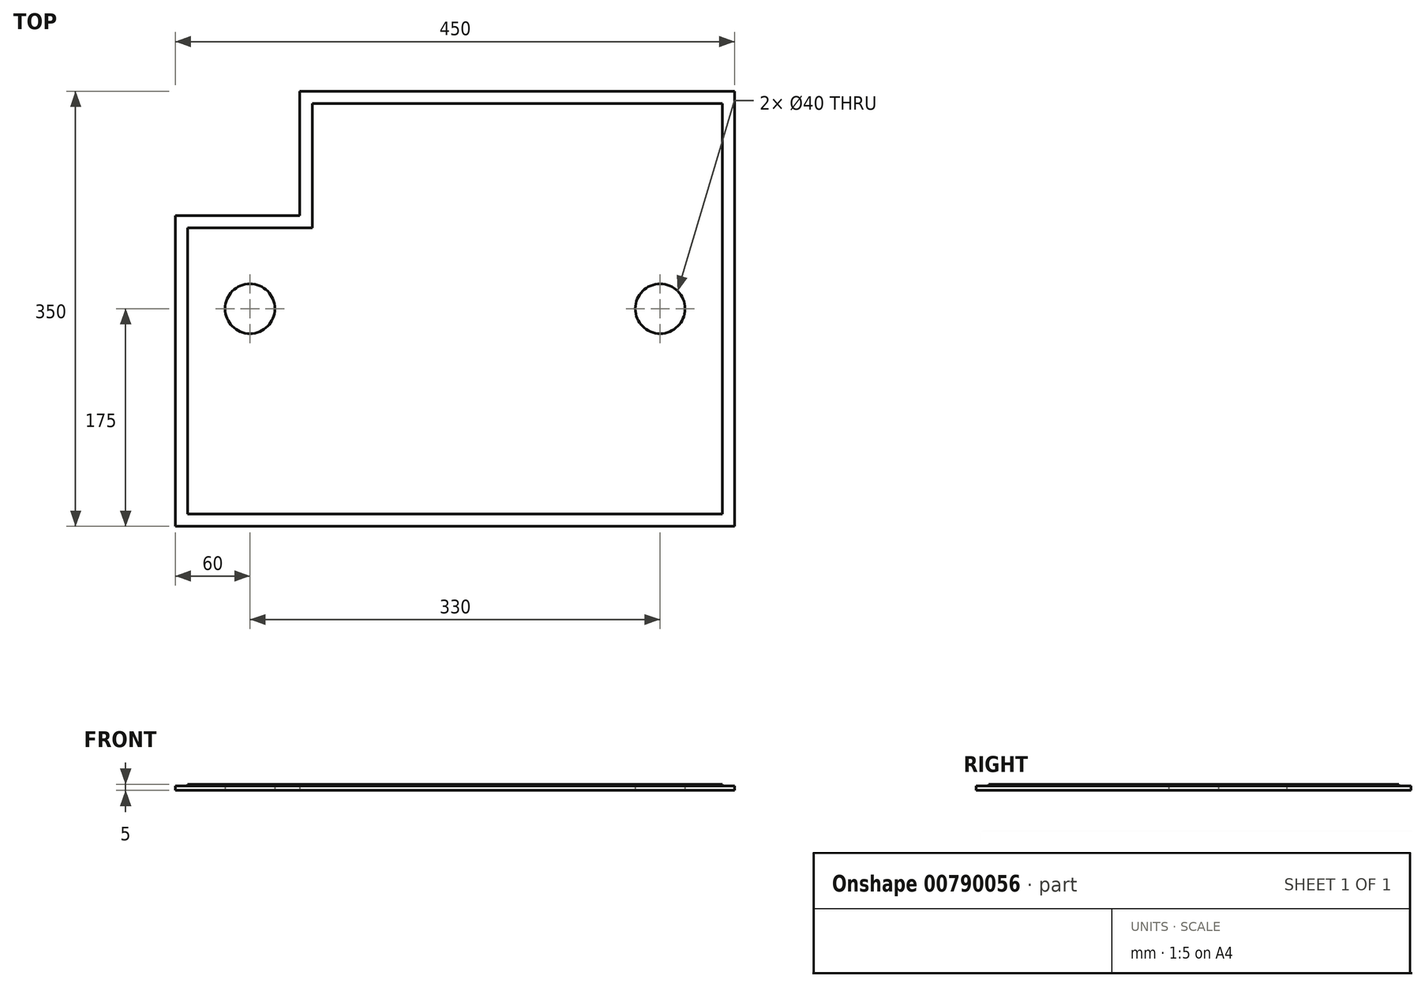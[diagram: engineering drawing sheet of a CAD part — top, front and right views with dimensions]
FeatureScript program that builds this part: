
annotation { "Feature Type Name" : "Feature", "Feature Type Description" : "" }
export const myFeature = defineFeature(function(context is Context, id is Id, definition is map)
    precondition{}
    {
        {
            var Q0;
            Q0=qCreatedBy(makeId("Top.planeOp"),FACE);
            var sketch = newSketch(context, id + "F0", { "sketchPlane" : qUnion([Q0])});
            skLineSegment(sketch, "E0", {"start": v(0, 0) * mm, "end": v(450, 0) * mm});
            skLineSegment(sketch, "E1", {"start": v(450, 0) * mm, "end": v(450, 350) * mm});
            skLineSegment(sketch, "E2", {"start": v(450, 350) * mm, "end": v(100, 350) * mm});
            skLineSegment(sketch, "E3", {"start": v(100, 350) * mm, "end": v(100, 250) * mm});
            skLineSegment(sketch, "E4", {"start": v(100, 250) * mm, "end": v(0, 250) * mm});
            skLineSegment(sketch, "E5", {"start": v(0, 250) * mm, "end": v(0, 0) * mm});
            skCircle(sketch, "E6", {"center": v(390, 175) * mm, "radius": 20 * mm});
            skPoint(sketch, "E6.centerSnap0", {"position": v(450, 175) * mm});
            skCircle(sketch, "E7", {"center": v(60, 175) * mm, "radius": 20 * mm});
            skLineSegment(sketch, "E8.0", {"start": v(440, 10) * mm, "end": v(440, 340) * mm});
            skLineSegment(sketch, "E8.1", {"start": v(110, 340) * mm, "end": v(110, 240) * mm});
            skLineSegment(sketch, "E8.2", {"start": v(110, 240) * mm, "end": v(10, 240) * mm});
            skLineSegment(sketch, "E8.3", {"start": v(440, 340) * mm, "end": v(110, 340) * mm});
            skLineSegment(sketch, "E8.4", {"start": v(10, 240) * mm, "end": v(10, 10) * mm});
            skLineSegment(sketch, "E8.5", {"start": v(10, 10) * mm, "end": v(440, 10) * mm});
            skSolve(sketch);
        }
        {
            var Q0;
            Q0=makeQuery(id+"F0.imprint","IMPRINT",FACE,{"disambiguationData":[TD([[makeQuery(id+"F0.imprint","IMPRINT",EDGE,{"derivedFrom":sQuery(id+"F0.wireOp",EDGE,"E6")}),-1.0]])]});
            extrude(context, id + "F1", {"entities" : qUnion([Q0]), "depth" : 5 * mm, "offsetDistance" : 25 * mm});
        }
        {
            var Q0;
            Q0=makeQuery(id+"F0.imprint","IMPRINT",FACE,{"disambiguationData":[TD([[makeQuery(id+"F0.imprint","IMPRINT",EDGE,{"derivedFrom":sQuery(id+"F0.wireOp",EDGE,"E0")}),1.0]])]});
            extrude(context, id + "F2", {"entities" : qUnion([Q0]), "operationType" : NewBodyOperationType.ADD, "depth" : 3.5 * mm, "offsetDistance" : 25 * mm});
        }
    });
